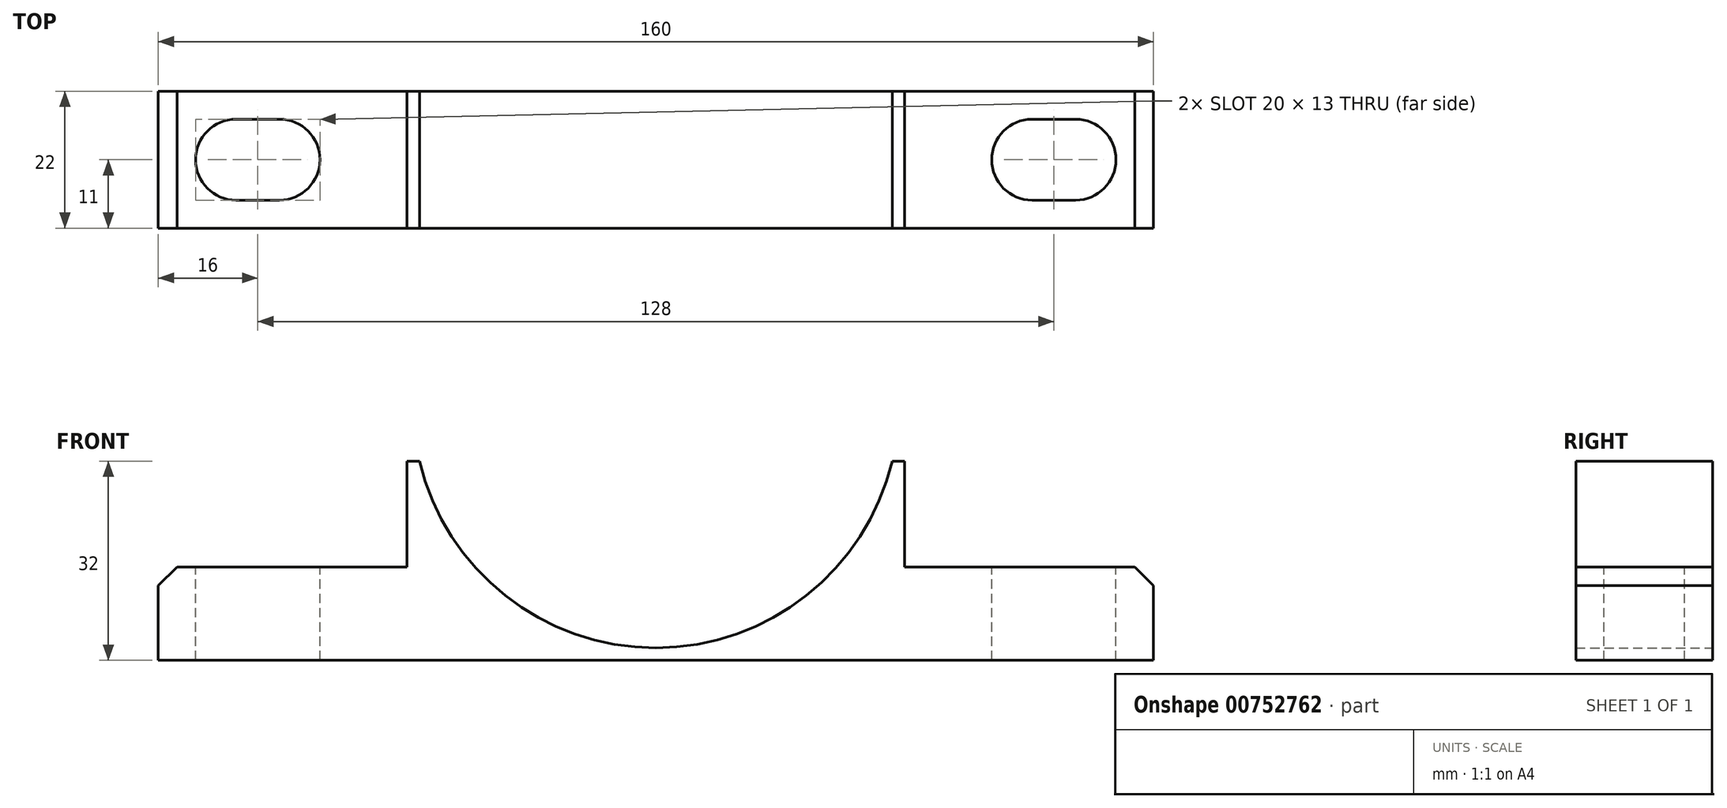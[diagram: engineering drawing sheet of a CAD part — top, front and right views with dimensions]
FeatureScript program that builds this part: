
annotation { "Feature Type Name" : "Feature", "Feature Type Description" : "" }
export const myFeature = defineFeature(function(context is Context, id is Id, definition is map)
    precondition{}
    {
        {
            var Q0;
            Q0=qCreatedBy(makeId("Front.planeOp"),FACE);
            var sketch = newSketch(context, id + "F0", { "sketchPlane" : qUnion([Q0])});
            skLineSegment(sketch, "E0.bottom", {"start": v(80, -7.5) * mm, "end": v(-80, -7.5) * mm});
            skLineSegment(sketch, "E0.left", {"start": v(80, -7.5) * mm, "end": v(80, 7.5) * mm});
            skLineSegment(sketch, "E0.right", {"start": v(-80, -7.5) * mm, "end": v(-80, 7.5) * mm});
            skPoint(sketch, "E0.middle", {"position": v(0, 0) * mm});
            skLineSegment(sketch, "E1", {"start": v(-40, 7.5) * mm, "end": v(-40, 24.5) * mm});
            skLineSegment(sketch, "E2", {"start": v(-40, 24.5) * mm, "end": v(-38, 24.5) * mm});
            skArc(sketch, "E3", {"start": v(-38, 24.5) * mm, "mid": v(0, -5.5) * mm, "end": v(38, 24.5) * mm});
            skPoint(sketch, "E4", {"position": v(0, -5.5) * mm});
            skLineSegment(sketch, "E5", {"start": v(0, 24.65) * mm, "end": v(0, 14.6) * mm, "construction": true});
            skLineSegment(sketch, "E6.MirrorCS", {"start": v(40, 7.5) * mm, "end": v(40, 24.5) * mm});
            skLineSegment(sketch, "E7.MirrorCS", {"start": v(40, 24.5) * mm, "end": v(38, 24.5) * mm});
            skLineSegment(sketch, "E8.trimOffspring", {"start": v(-40, 7.5) * mm, "end": v(-80, 7.5) * mm});
            skLineSegment(sketch, "E9", {"start": v(40, 7.5) * mm, "end": v(80, 7.5) * mm});
            skSolve(sketch);
        }
        {
            var Q0;
            Q0 = qSketchRegion(id + "F0", true);
            extrude(context, id + "F1", {"entities" : qUnion([Q0]), "depth" : 22 * mm, "offsetDistance" : 25 * mm});
        }
        {
            var Q0;
            Q0=makeQuery(id+"F1.opExtrude","SWEPT_EDGE",EDGE,{"disambiguationData":[OSD([sQuery(id+"F0.wireOp",EDGE,"E0.right"),sQuery(id+"F0.wireOp",EDGE,"E8.trimOffspring")])]});
            var Q1;
            Q1=makeQuery(id+"F1.opExtrude","SWEPT_EDGE",EDGE,{"disambiguationData":[OSD([sQuery(id+"F0.wireOp",EDGE,"E0.left"),sQuery(id+"F0.wireOp",EDGE,"E9")])]});
            chamfer(context, id + "F2", {"entities" : qUnion([Q0, Q1]), "width" : 3 * mm, "tangentPropagation" : true});
        }
        {
            var Q0;
            Q0=makeQuery(id+"F1.opExtrude","SWEPT_FACE",FACE,{"disambiguationData":[OSD([sQuery(id+"F0.wireOp",EDGE,"E8.trimOffspring")])]});
            var sketch = newSketch(context, id + "F3", { "sketchPlane" : qUnion([Q0])});
            skArc(sketch, "E10", {"start": v(-67.5, -4.5) * mm, "mid": v(-74, -11) * mm, "end": v(-67.5, -17.5) * mm});
            skPoint(sketch, "E10.centerSnap0", {"position": v(-77, -11) * mm});
            skArc(sketch, "E11", {"start": v(-60.5, -17.5) * mm, "mid": v(-54, -11) * mm, "end": v(-60.5, -4.5) * mm});
            skLineSegment(sketch, "E12", {"start": v(-67.5, -4.5) * mm, "end": v(-60.5, -4.5) * mm});
            skLineSegment(sketch, "E13", {"start": v(-67.5, -17.5) * mm, "end": v(-60.5, -17.5) * mm});
            skPoint(sketch, "E14", {"position": v(-74, -11) * mm});
            skPoint(sketch, "E15", {"position": v(-54, -11) * mm});
            skLineSegment(sketch, "E16", {"start": v(0, 0) * mm, "end": v(0, -15.12) * mm, "construction": true});
            skArc(sketch, "E17.MirrorCS", {"start": v(60.5, -17.5) * mm, "mid": v(54, -11) * mm, "end": v(60.5, -4.5) * mm});
            skLineSegment(sketch, "E18.MirrorCS", {"start": v(67.5, -4.5) * mm, "end": v(60.5, -4.5) * mm});
            skArc(sketch, "E19.MirrorCS", {"start": v(67.5, -4.5) * mm, "mid": v(74, -11) * mm, "end": v(67.5, -17.5) * mm});
            skLineSegment(sketch, "E20.MirrorCS", {"start": v(67.5, -17.5) * mm, "end": v(60.5, -17.5) * mm});
            skSolve(sketch);
        }
        {
            var Q0;
            Q0 = qSketchRegion(id + "F3", true);
            extrude(context, id + "F4", {"entities" : qUnion([Q0]), "operationType" : NewBodyOperationType.REMOVE, "endBound" : BoundingType.THROUGH_ALL, "oppositeDirection" : true, "depth" : 25 * mm, "offsetDistance" : 25 * mm});
        }
    });
